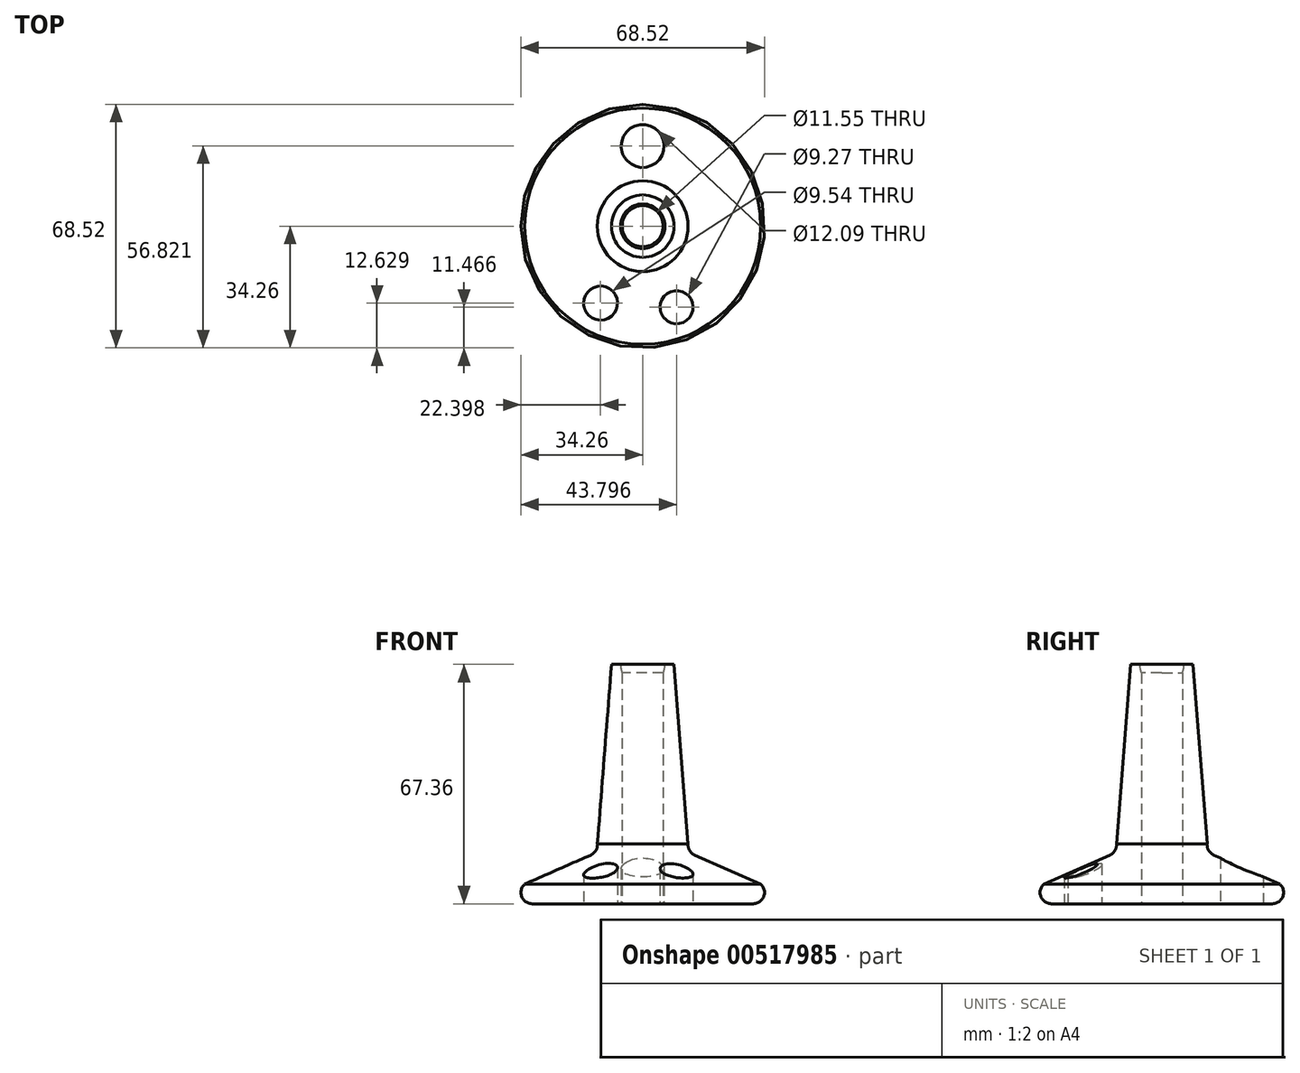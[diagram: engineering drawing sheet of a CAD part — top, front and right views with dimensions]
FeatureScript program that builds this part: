
annotation { "Feature Type Name" : "Feature", "Feature Type Description" : "" }
export const myFeature = defineFeature(function(context is Context, id is Id, definition is map)
    precondition{}
    {
        {
            var Q0;
            Q0=qCreatedBy(makeId("Front.planeOp"),FACE);
            var sketch = newSketch(context, id + "F0", { "sketchPlane" : qUnion([Q0])});
            skLineSegment(sketch, "E0", {"start": v(0, 0) * mm, "end": v(0, 61.1) * mm});
            skLineSegment(sketch, "E1", {"start": v(6.25, 67.36) * mm, "end": v(8.79, 67.36) * mm});
            skLineSegment(sketch, "E2", {"start": v(0, 0) * mm, "end": v(31.09, 0) * mm});
            skArc(sketch, "E3", {"start": v(31.09, 0) * mm, "mid": v(34.05, 2.04) * mm, "end": v(33.2, 5.54) * mm});
            skLineSegment(sketch, "E4", {"start": v(33.2, 5.54) * mm, "end": v(14.64, 13.7) * mm});
            skPoint(sketch, "E5.start.orphan", {"position": v(6.43, 5.54) * mm});
            skArc(sketch, "E6", {"start": v(12.76, 16.9) * mm, "mid": v(13.18, 15) * mm, "end": v(14.64, 13.7) * mm});
            skLineSegment(sketch, "E7", {"start": v(12.76, 16.9) * mm, "end": v(8.79, 67.36) * mm});
            skArc(sketch, "E8", {"start": v(0, 61.1) * mm, "mid": v(4.42, 62.94) * mm, "end": v(6.25, 67.36) * mm});
            skSolve(sketch);
        }
        {
            var Q0;
            Q0=makeQuery(id+"F0.imprint","IMPRINT",FACE,{"disambiguationData":[TD([[makeQuery(id+"F0.imprint","IMPRINT",EDGE,{"derivedFrom":sQuery(id+"F0.wireOp",EDGE,"E0")}),-1.0]])]});
            var Q1;
            Q1=sQuery(id+"F0.wireOp",EDGE,"E0");
            revolve(context, id + "F1", {"entities" : qUnion([Q0]), "axis" : qUnion([Q1]), "revolveType" : RevolveType.FULL});
        }
        {
            var Q0;
            Q0=makeQuery(id+"F1.opRevolve","SWEPT_FACE",FACE,{"disambiguationData":[OSD([sQuery(id+"F0.wireOp",EDGE,"E2")])]});
            var sketch = newSketch(context, id + "F2", { "sketchPlane" : qUnion([Q0])});
            skCircle(sketch, "E9", {"center": v(0, 0) * mm, "radius": 5.78 * mm});
            skCircle(sketch, "E10", {"center": v(-20, -9.3) * mm, "radius": 6.98 * mm});
            skCircle(sketch, "E11", {"center": v(10.47, 19.54) * mm, "radius": 4.79 * mm});
            skCircle(sketch, "E12", {"center": v(11.16, -17.44) * mm, "radius": 5.89 * mm});
            skSolve(sketch);
        }
        {
            var Q0;
            Q0=makeQuery(id+"F2.imprint","IMPRINT",FACE,{"disambiguationData":[TD([[makeQuery(id+"F2.imprint","IMPRINT",EDGE,{"derivedFrom":sQuery(id+"F2.wireOp",EDGE,"E9")}),1.0]])]});
            extrude(context, id + "F3", {"entities" : qUnion([Q0]), "operationType" : NewBodyOperationType.REMOVE, "oppositeDirection" : true, "depth" : 87.88 * mm, "offsetDistance" : 25.4 * mm});
        }
        {
            var Q0;
            Q0=makeQuery(id+"F1.opRevolve","SWEPT_FACE",FACE,{"disambiguationData":[OSD([sQuery(id+"F0.wireOp",EDGE,"E2")])]});
            var sketch = newSketch(context, id + "F4", { "sketchPlane" : qUnion([Q0])});
            skCircle(sketch, "E13", {"center": v(9.54, 22.8) * mm, "radius": 4.63 * mm});
            skCircle(sketch, "E14", {"center": v(-11.86, 21.63) * mm, "radius": 4.77 * mm});
            skCircle(sketch, "E15", {"center": v(0, -22.56) * mm, "radius": 6.05 * mm});
            skSolve(sketch);
        }
        {
            var Q0;
            Q0=makeQuery(id+"F4.imprint","IMPRINT",FACE,{"disambiguationData":[TD([[makeQuery(id+"F4.imprint","IMPRINT",EDGE,{"derivedFrom":sQuery(id+"F4.wireOp",EDGE,"E13")}),1.0]])]});
            var Q1;
            Q1=makeQuery(id+"F4.imprint","IMPRINT",FACE,{"disambiguationData":[TD([[makeQuery(id+"F4.imprint","IMPRINT",EDGE,{"derivedFrom":sQuery(id+"F4.wireOp",EDGE,"E14")}),1.0]])]});
            var Q2;
            Q2=makeQuery(id+"F4.imprint","IMPRINT",FACE,{"disambiguationData":[TD([[makeQuery(id+"F4.imprint","IMPRINT",EDGE,{"derivedFrom":sQuery(id+"F4.wireOp",EDGE,"E15")}),1.0]])]});
            extrude(context, id + "F5", {"entities" : qUnion([Q0, Q1, Q2]), "operationType" : NewBodyOperationType.REMOVE, "oppositeDirection" : true, "depth" : 25.4 * mm, "offsetDistance" : 25.4 * mm});
        }
    });
